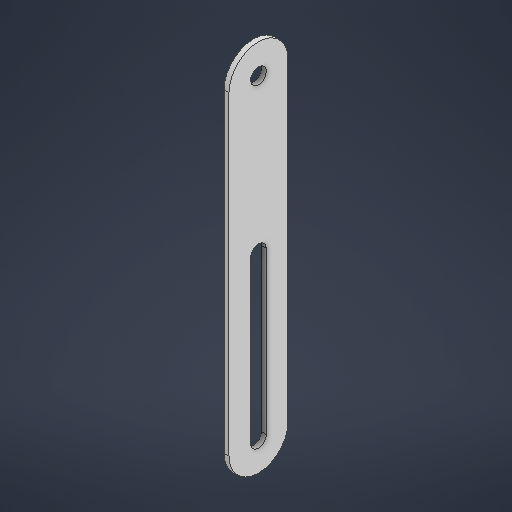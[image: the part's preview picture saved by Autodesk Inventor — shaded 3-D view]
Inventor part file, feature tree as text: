
AUTODESK INVENTOR PART (.ipt)
format: ipt  version: 2025.2 (Build 292293000, 293)  size: 195,072 bytes
history: native  units: in
note: dims shown in document units (in); Inventor stores cm internally (conversion verified against a paired STEP export)
features: extrude x1, sketch x1
ambient origin geometry x8: Origin, YZ Plane, XZ Plane, XY Plane, X Axis, Y Axis, Z Axis, Center Point
bodies: Solid1 (feature_tree)
feature tree (2):
  extrude  "Extrusion1"  Depth=0.0625in TaperAngle=0.0deg
  sketch  "Sketch1"  dims[d0=0.2in d7=0.0625in d8=0.0in d12=0.2in d17=2.05in]
